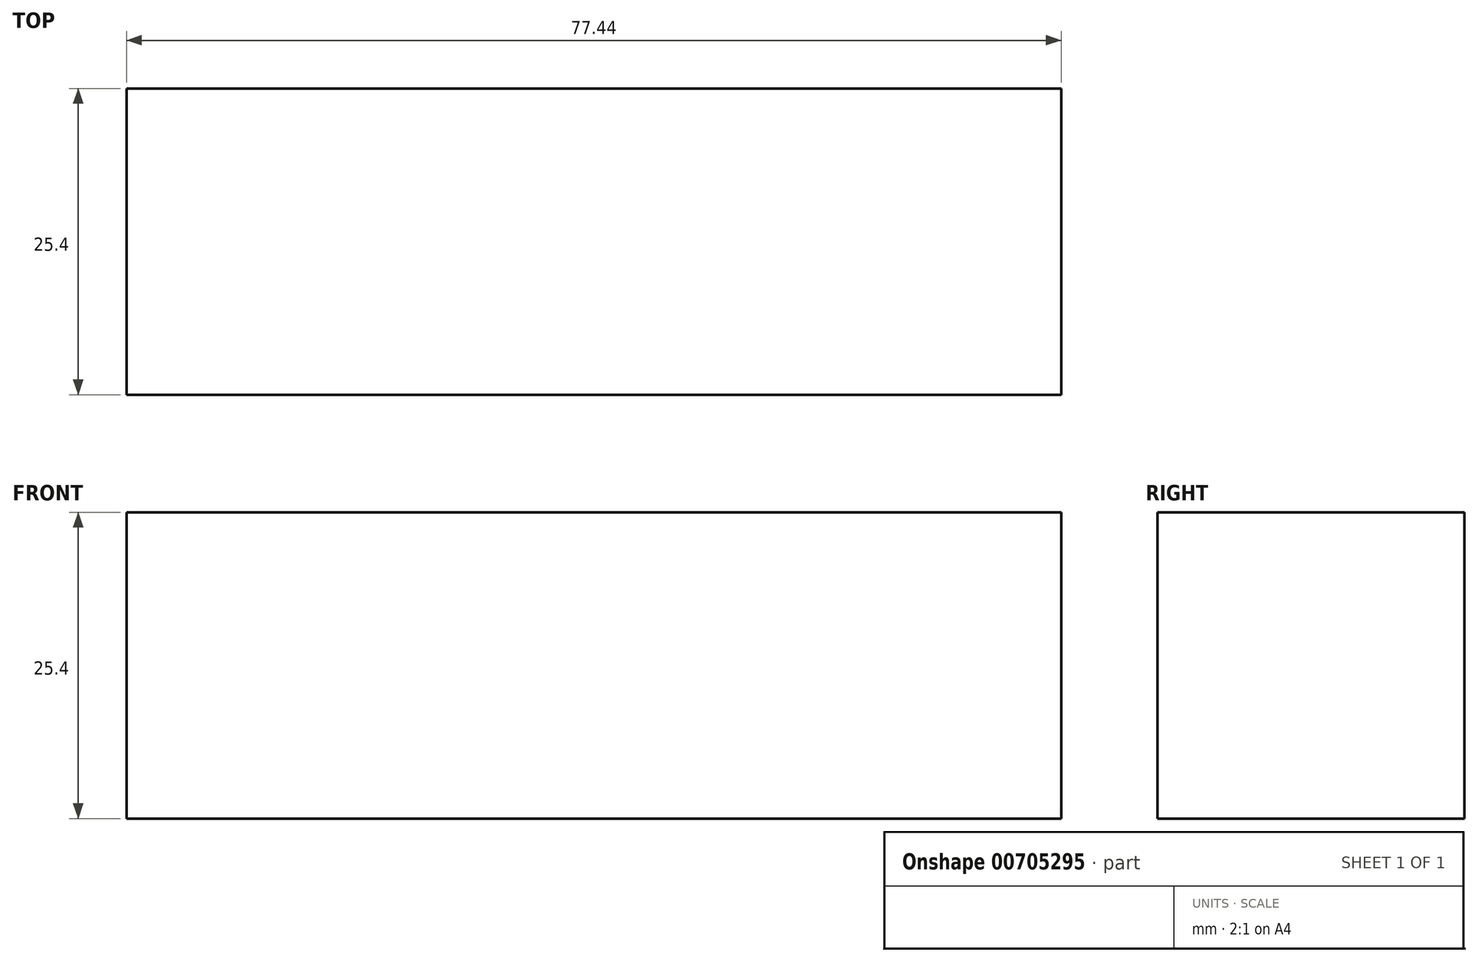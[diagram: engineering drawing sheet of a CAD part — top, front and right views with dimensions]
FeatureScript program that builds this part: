
annotation { "Feature Type Name" : "Feature", "Feature Type Description" : "" }
export const myFeature = defineFeature(function(context is Context, id is Id, definition is map)
    precondition{}
    {
        {
            var Q0;
            Q0=qCreatedBy(makeId("Front.planeOp"),FACE);
            var sketch = newSketch(context, id + "F0", { "sketchPlane" : qUnion([Q0])});
            skLineSegment(sketch, "E0.bottom", {"start": v(0, 0) * mm, "end": v(-26.64, 0) * mm});
            skLineSegment(sketch, "E0.top", {"start": v(0, 25.4) * mm, "end": v(-26.64, 25.4) * mm});
            skLineSegment(sketch, "E0.left", {"start": v(0, 0) * mm, "end": v(0, 25.4) * mm});
            skLineSegment(sketch, "E0.right", {"start": v(-26.64, 0) * mm, "end": v(-26.64, 25.4) * mm});
            skLineSegment(sketch, "E1.bottom", {"start": v(-26.64, 25.4) * mm, "end": v(-52.04, 25.4) * mm});
            skLineSegment(sketch, "E1.top", {"start": v(-26.64, 0) * mm, "end": v(-52.04, 0) * mm});
            skLineSegment(sketch, "E1.left", {"start": v(-26.64, 25.4) * mm, "end": v(-26.64, 0) * mm});
            skLineSegment(sketch, "E1.right", {"start": v(-52.04, 25.4) * mm, "end": v(-52.04, 0) * mm});
            skLineSegment(sketch, "E2.bottom", {"start": v(0, 0) * mm, "end": v(25.4, 0) * mm});
            skLineSegment(sketch, "E2.top", {"start": v(0, 25.4) * mm, "end": v(25.4, 25.4) * mm});
            skLineSegment(sketch, "E2.right", {"start": v(25.4, 0) * mm, "end": v(25.4, 25.4) * mm});
            skLineSegment(sketch, "E3.bottom", {"start": v(-52.04, 25.4) * mm, "end": v(-26.64, 25.4) * mm});
            skLineSegment(sketch, "E3.top", {"start": v(-52.04, 50.8) * mm, "end": v(-26.64, 50.8) * mm});
            skLineSegment(sketch, "E3.left", {"start": v(-52.04, 25.4) * mm, "end": v(-52.04, 50.8) * mm});
            skLineSegment(sketch, "E3.right", {"start": v(-26.64, 25.4) * mm, "end": v(-26.64, 50.8) * mm});
            skLineSegment(sketch, "E4.bottom", {"start": v(25.4, 25.4) * mm, "end": v(0, 25.4) * mm});
            skLineSegment(sketch, "E4.top", {"start": v(25.4, 50.8) * mm, "end": v(0, 50.8) * mm});
            skLineSegment(sketch, "E4.left", {"start": v(25.4, 25.4) * mm, "end": v(25.4, 50.8) * mm});
            skLineSegment(sketch, "E4.right", {"start": v(0, 25.4) * mm, "end": v(0, 50.8) * mm});
            skLineSegment(sketch, "E5.bottom", {"start": v(0, 50.8) * mm, "end": v(25.4, 50.8) * mm});
            skLineSegment(sketch, "E5.top", {"start": v(0, 76.2) * mm, "end": v(25.4, 76.2) * mm});
            skLineSegment(sketch, "E5.left", {"start": v(0, 50.8) * mm, "end": v(0, 76.2) * mm});
            skLineSegment(sketch, "E5.right", {"start": v(25.4, 50.8) * mm, "end": v(25.4, 76.2) * mm});
            skSolve(sketch);
        }
        {
            var Q0;
            Q0=makeQuery(id+"F0.imprint","IMPRINT",FACE,{"disambiguationData":[TD([[makeQuery(id+"F0.imprint","IMPRINT",EDGE,{"derivedFrom":sQuery(id+"F0.wireOp",EDGE,"E0.bottom")}),-1.0]])]});
            var sketch = newSketch(context, id + "F1", { "sketchPlane" : qUnion([Q0])});
            skSolve(sketch);
        }
        {
            var Q0;
            Q0 = qSketchRegion(id + "F1", true);
            var Q1;
            Q1=makeQuery(id+"F0.imprint","IMPRINT",FACE,{"disambiguationData":[TD([[makeQuery(id+"F0.imprint","IMPRINT",EDGE,{"derivedFrom":sQuery(id+"F0.wireOp",EDGE,"E3.bottom")}),1.0]])]});
            var Q2;
            Q2=makeQuery(id+"F0.imprint","IMPRINT",FACE,{"disambiguationData":[TD([[makeQuery(id+"F0.imprint","IMPRINT",EDGE,{"derivedFrom":sQuery(id+"F0.wireOp",EDGE,"E1.top")}),-1.0]])]});
            var Q3;
            Q3=makeQuery(id+"F0.imprint","IMPRINT",FACE,{"disambiguationData":[TD([[makeQuery(id+"F0.imprint","IMPRINT",EDGE,{"derivedFrom":sQuery(id+"F0.wireOp",EDGE,"E0.bottom")}),-1.0]])]});
            var Q4;
            Q4=makeQuery(id+"F0.imprint","IMPRINT",FACE,{"disambiguationData":[TD([[makeQuery(id+"F0.imprint","IMPRINT",EDGE,{"derivedFrom":sQuery(id+"F0.wireOp",EDGE,"E5.bottom")}),1.0]])]});
            var Q5;
            Q5=makeQuery(id+"F0.imprint","IMPRINT",FACE,{"disambiguationData":[TD([[makeQuery(id+"F0.imprint","IMPRINT",EDGE,{"derivedFrom":sQuery(id+"F0.wireOp",EDGE,"E4.bottom")}),-1.0]])]});
            var Q6;
            Q6=makeQuery(id+"F0.imprint","IMPRINT",FACE,{"disambiguationData":[TD([[makeQuery(id+"F0.imprint","IMPRINT",EDGE,{"derivedFrom":sQuery(id+"F0.wireOp",EDGE,"E2.bottom")}),1.0]])]});
            extrude(context, id + "F2", {"entities" : qUnion([Q0, Q1, Q2, Q3, Q4, Q5, Q6]), "depth" : 25.4 * mm, "offsetDistance" : 25.4 * mm});
        }
    });
